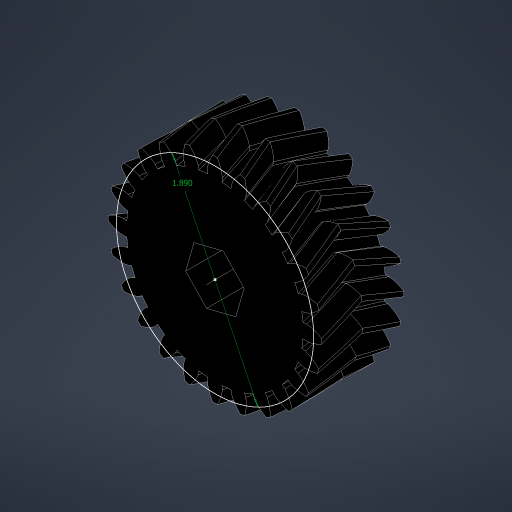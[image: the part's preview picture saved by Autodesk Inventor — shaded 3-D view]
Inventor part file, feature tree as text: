
AUTODESK INVENTOR PART (.ipt)
format: ipt  version: 2023.4 (Build 274418000, 418)  size: 866,304 bytes
history: native  units: in
note: dims shown in document units (in); Inventor stores cm internally (conversion verified against a paired STEP export)
features: sketch x2, extrude x1, other x1
ambient origin geometry x8: Origin, YZ Plane, XZ Plane, XY Plane, X Axis, Y Axis, Z Axis, Center Point
bodies: Solid1 (feature_tree)
feature tree (4):
  extrude  "Extrusion1"  TaperAngle=0.0deg  [1 undecoded]
  sketch  "Sketch3"  dims[d5=1.8898in]
  sketch  "Sketch1"  dims[d0=0.5in d1=0.0in d2=0.0in]
  other  "Helical 2M 24T"
note: 1 required parameter value undecoded (feature->parameter linkage not recoverable at this tier; creation-order binding heuristic only, values carry confidence <= 0.55)
